# Revit family: Shower-Handshower-KOHLER-MasterShower-K-8520
name_source: partatom
category: Plumbing Fixtures
revit_build: Autodesk Revit 2015 (Build: 20140606_1530(x64)
units: mm (PartAtom-declared; Revit-internal decimal feet)

## types (2) — shared parameters
ADA = No
Assembly Code = D2010700
CW Connection = No
Cold Water Inlet = Cold Water Inlet
Date Modified = 03/07/2018
Default Elevation = 36"
Description = Hotel Handshower Kit
HW Connection = Yes
Height = 37 5/8"
Hot Water Inlet = Hot Water Inlet
Length = 7 1/2"
Manufacturer = KOHLER Co.
MasterFormat 1995 = 15410
MasterFormat 2004 = 22.41.23
Material = Premium Metal
Panel Thickness = 0"
Product Documentation Link = http://www.us.kohler.com
Product Name = MasterShower
Product Page URL = http://www.us.kohler.com
URL = https://www.us.kohler.com
Vent Connection = No
Waste Connection = No
Waste Water Outlet = Waste Water Outlet
Width = 17"

## per-type parameters (varying)
| type | Finish | Model | Type |
| CP- Polished Chrome | Kohler-Metal-CP-Polished_Chrome | K-8520-CP | 1 |
| PB- Vibrant Polished Brass | Kohler-Metal-PB-Vibrant_Polished_Brass | K-8520-PB | 2 |

## geometry (parser evidence)
native form markers: Blend x2, Sweep x4
no freeform markers — native parametric forms only
